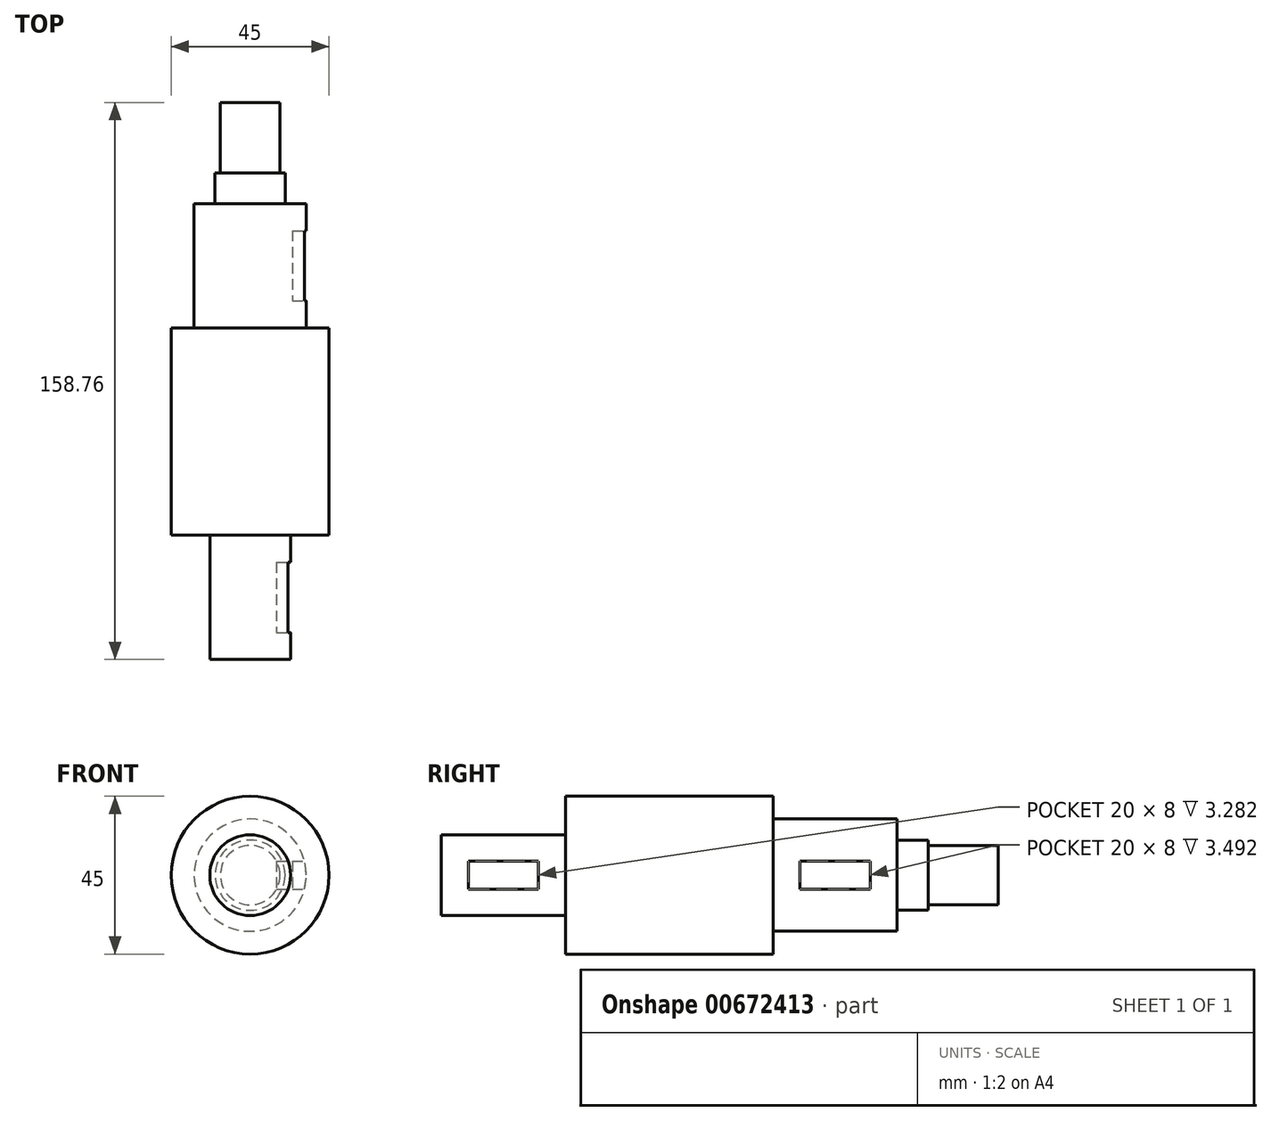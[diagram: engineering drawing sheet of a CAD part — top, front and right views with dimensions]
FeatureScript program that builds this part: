
annotation { "Feature Type Name" : "Feature", "Feature Type Description" : "" }
export const myFeature = defineFeature(function(context is Context, id is Id, definition is map)
    precondition{}
    {
        {
            var Q0;
            Q0=qCreatedBy(makeId("Front.planeOp"),FACE);
            var sketch = newSketch(context, id + "F0", { "sketchPlane" : qUnion([Q0])});
            skCircle(sketch, "E0", {"center": v(0, 0) * mm, "radius": 8.5 * mm});
            skSolve(sketch);
        }
        {
            var Q0;
            Q0 = qSketchRegion(id + "F0", true);
            extrude(context, id + "F1", {"entities" : qUnion([Q0]), "depth" : 20 * mm, "offsetDistance" : 25.4 * mm});
        }
        {
            var Q0;
            Q0=makeQuery(id+"F1.opExtrude","CAP_FACE",FACE,{"disambiguationData":[OSD([sQuery(id+"F0.wireOp",EDGE,"E0")])],"isStart":false});
            var sketch = newSketch(context, id + "F2", { "sketchPlane" : qUnion([Q0])});
            skCircle(sketch, "E1", {"center": v(0, 0) * mm, "radius": 10 * mm});
            skSolve(sketch);
        }
        {
            var Q0;
            Q0 = qSketchRegion(id + "F2", true);
            extrude(context, id + "F3", {"entities" : qUnion([Q0]), "operationType" : NewBodyOperationType.ADD, "depth" : 8.83 * mm, "offsetDistance" : 25.4 * mm});
        }
        {
            var Q0;
            Q0=makeQuery(id+"F3.opExtrude","CAP_FACE",FACE,{"disambiguationData":[OSD([sQuery(id+"F2.wireOp",EDGE,"E1")])],"isStart":false});
            var sketch = newSketch(context, id + "F4", { "sketchPlane" : qUnion([Q0])});
            skCircle(sketch, "E2", {"center": v(0, 0) * mm, "radius": 16 * mm});
            skSolve(sketch);
        }
        {
            var Q0;
            Q0 = qSketchRegion(id + "F4", true);
            extrude(context, id + "F5", {"entities" : qUnion([Q0]), "operationType" : NewBodyOperationType.ADD, "depth" : 35.4 * mm, "offsetDistance" : 25.4 * mm});
        }
        {
            var Q0;
            Q0=makeQuery(id+"F5.opExtrude","CAP_FACE",FACE,{"disambiguationData":[OSD([sQuery(id+"F4.wireOp",EDGE,"E2")])],"isStart":false});
            var sketch = newSketch(context, id + "F6", { "sketchPlane" : qUnion([Q0])});
            skCircle(sketch, "E3", {"center": v(0, 0) * mm, "radius": 22.5 * mm});
            skSolve(sketch);
        }
        {
            var Q0;
            Q0 = qSketchRegion(id + "F6", true);
            extrude(context, id + "F7", {"entities" : qUnion([Q0]), "operationType" : NewBodyOperationType.ADD, "depth" : 59.13 * mm, "offsetDistance" : 25.4 * mm});
        }
        {
            var Q0;
            Q0=makeQuery(id+"F7.opExtrude","CAP_FACE",FACE,{"disambiguationData":[OSD([sQuery(id+"F6.wireOp",EDGE,"E3")])],"isStart":false});
            var sketch = newSketch(context, id + "F8", { "sketchPlane" : qUnion([Q0])});
            skCircle(sketch, "E4", {"center": v(0, 0) * mm, "radius": 11.5 * mm});
            skSolve(sketch);
        }
        {
            var Q0;
            Q0 = qSketchRegion(id + "F8", true);
            extrude(context, id + "F9", {"entities" : qUnion([Q0]), "operationType" : NewBodyOperationType.ADD, "depth" : 35.4 * mm, "offsetDistance" : 25.4 * mm});
        }
        {
            var Q0;
            Q0=qCreatedBy(makeId("Right.planeOp"),FACE);
            var sketch = newSketch(context, id + "F10", { "sketchPlane" : qUnion([Q0])});
            skLineSegment(sketch, "E5.0", {"start": v(-64.23, -22.5) * mm, "end": v(-64.23, 22.5) * mm});
            skLineSegment(sketch, "E6.0", {"start": v(-28.83, -16) * mm, "end": v(-28.83, 16) * mm});
            skLineSegment(sketch, "E7", {"start": v(-28.83, 0) * mm, "end": v(-64.23, 0) * mm});
            skLineSegment(sketch, "E8.bottom", {"start": v(-36.53, 4) * mm, "end": v(-56.53, 4) * mm});
            skLineSegment(sketch, "E8.top", {"start": v(-36.53, -4) * mm, "end": v(-56.53, -4) * mm});
            skLineSegment(sketch, "E8.left", {"start": v(-36.53, 4) * mm, "end": v(-36.53, -4) * mm});
            skLineSegment(sketch, "E8.right", {"start": v(-56.53, 4) * mm, "end": v(-56.53, -4) * mm});
            skPoint(sketch, "E8.middle", {"position": v(-46.53, 0) * mm});
            skSolve(sketch);
        }
        {
            var Q0;
            Q0=qCreatedBy(makeId("Right.planeOp"),FACE);
            cPlane(context, id + "F11", {"entities" : qUnion([Q0]), "cplaneType" : CPlaneType.OFFSET, "offset" : 11.5 * mm, "width" : 152.4 * mm, "height" : 152.4 * mm});
        }
        {
            var Q0;
            Q0=qCreatedBy(id+"F11.planeOp",FACE);
            var sketch = newSketch(context, id + "F12", { "sketchPlane" : qUnion([Q0])});
            skLineSegment(sketch, "E9.0", {"start": v(-123.36, -22.5) * mm, "end": v(-123.36, 22.5) * mm});
            skLineSegment(sketch, "E10.0", {"start": v(-158.76, -11.5) * mm, "end": v(-158.76, 11.5) * mm});
            skLineSegment(sketch, "E11", {"start": v(-158.76, 0) * mm, "end": v(-123.36, 0) * mm});
            skLineSegment(sketch, "E12.bottom", {"start": v(-131.06, 4) * mm, "end": v(-151.06, 4) * mm});
            skLineSegment(sketch, "E12.top", {"start": v(-131.06, -4) * mm, "end": v(-151.06, -4) * mm});
            skLineSegment(sketch, "E12.left", {"start": v(-131.06, 4) * mm, "end": v(-131.06, -4) * mm});
            skLineSegment(sketch, "E12.right", {"start": v(-151.06, 4) * mm, "end": v(-151.06, -4) * mm});
            skPoint(sketch, "E12.middle", {"position": v(-141.06, 0) * mm});
            skSolve(sketch);
        }
        {
            var Q0;
            Q0 = qSketchRegion(id + "F12", true);
            extrude(context, id + "F13", {"entities" : qUnion([Q0]), "operationType" : NewBodyOperationType.REMOVE, "oppositeDirection" : true, "depth" : 4 * mm, "offsetDistance" : 25.4 * mm});
        }
        {
            var Q0;
            Q0=qCreatedBy(makeId("Right.planeOp"),FACE);
            cPlane(context, id + "F14", {"entities" : qUnion([Q0]), "cplaneType" : CPlaneType.OFFSET, "offset" : 16 * mm, "width" : 152.4 * mm, "height" : 152.4 * mm});
        }
        {
            var Q0;
            Q0=qCreatedBy(id+"F14.planeOp",FACE);
            var sketch = newSketch(context, id + "F15", { "sketchPlane" : qUnion([Q0])});
            skLineSegment(sketch, "E13.0", {"start": v(-64.23, -22.5) * mm, "end": v(-64.23, 22.5) * mm});
            skLineSegment(sketch, "E14.0", {"start": v(-28.83, -16) * mm, "end": v(-28.83, 16) * mm});
            skLineSegment(sketch, "E15", {"start": v(-28.83, 0) * mm, "end": v(-64.23, 0) * mm});
            skLineSegment(sketch, "E16.bottom", {"start": v(-36.53, 4) * mm, "end": v(-56.53, 4) * mm});
            skLineSegment(sketch, "E16.top", {"start": v(-36.53, -4) * mm, "end": v(-56.53, -4) * mm});
            skLineSegment(sketch, "E16.left", {"start": v(-36.53, 4) * mm, "end": v(-36.53, -4) * mm});
            skLineSegment(sketch, "E16.right", {"start": v(-56.53, 4) * mm, "end": v(-56.53, -4) * mm});
            skPoint(sketch, "E16.middle", {"position": v(-46.53, 0) * mm});
            skSolve(sketch);
        }
        {
            var Q0;
            Q0 = qSketchRegion(id + "F15", true);
            extrude(context, id + "F16", {"entities" : qUnion([Q0]), "operationType" : NewBodyOperationType.REMOVE, "oppositeDirection" : true, "depth" : 4 * mm, "offsetDistance" : 25.4 * mm});
        }
    });
